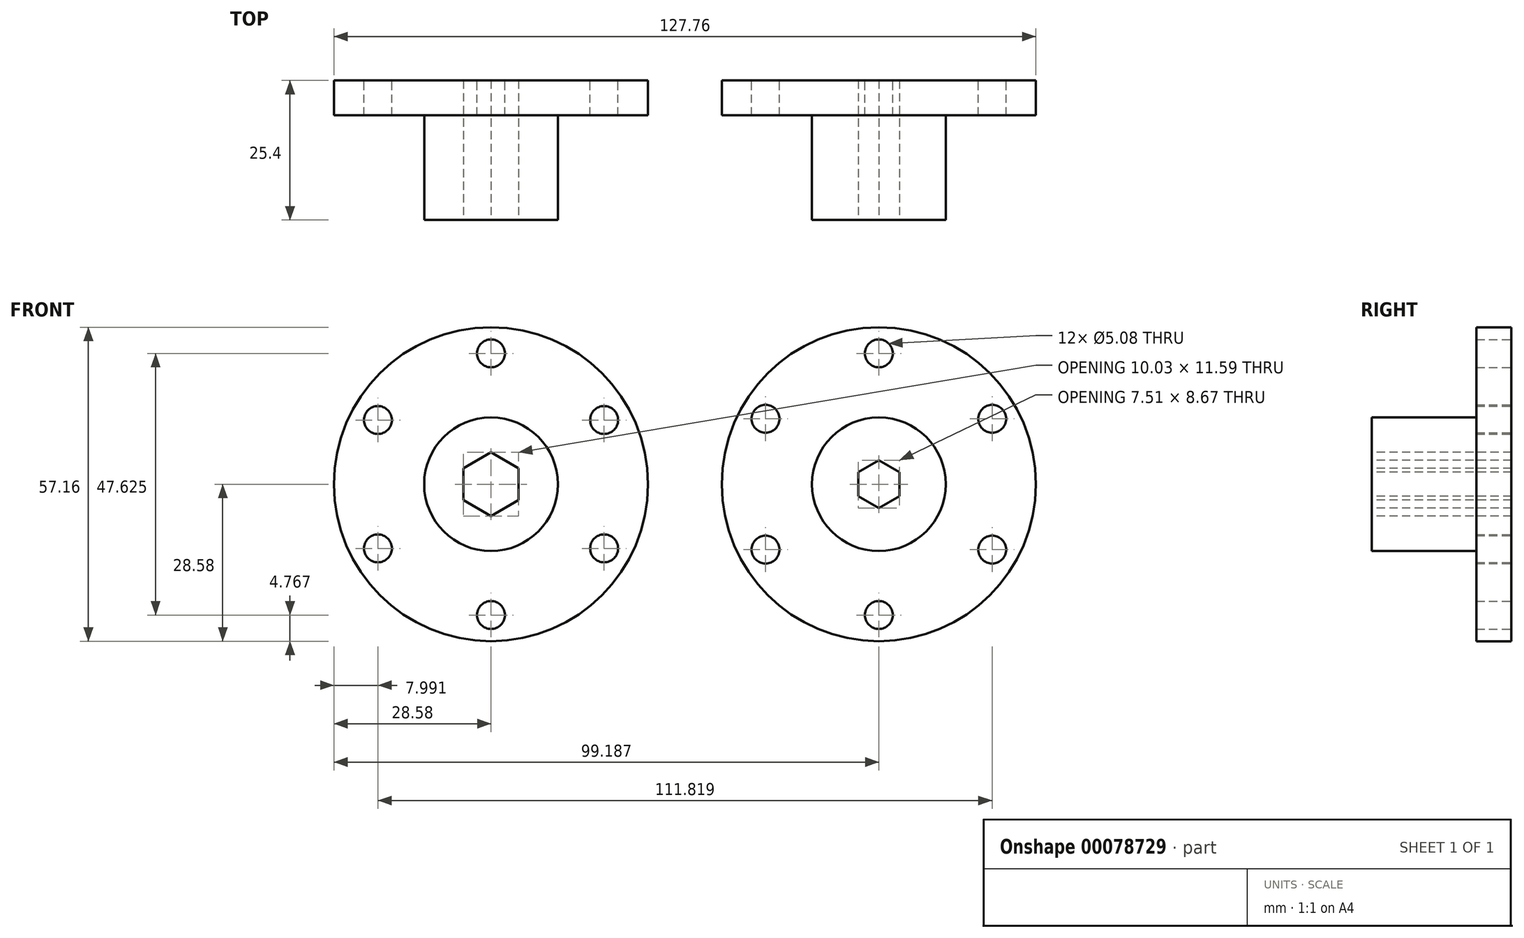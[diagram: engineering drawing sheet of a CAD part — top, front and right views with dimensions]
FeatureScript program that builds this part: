
annotation { "Feature Type Name" : "Feature", "Feature Type Description" : "" }
export const myFeature = defineFeature(function(context is Context, id is Id, definition is map)
    precondition{}
    {
        {
            var Q0;
            Q0=qCreatedBy(makeId("Front.planeOp"),FACE);
            var sketch = newSketch(context, id + "F0", { "sketchPlane" : qUnion([Q0])});
            skCircle(sketch, "E0", {"center": v(0, 0) * mm, "radius": 28.58 * mm});
            skCircle(sketch, "E1", {"center": v(0, 23.81) * mm, "radius": 2.54 * mm});
            skLineSegment(sketch, "E2", {"start": v(0, 23.81) * mm, "end": v(0, 0) * mm, "construction": true});
            skLineSegment(sketch, "E3", {"start": v(0, 0) * mm, "end": v(46.34, 26.76) * mm, "construction": true});
            skCircle(sketch, "E4", {"center": v(0, 0) * mm, "radius": 23.81 * mm, "construction": true});
            skCircle(sketch, "E5", {"center": v(20.59, 11.68) * mm, "radius": 2.54 * mm});
            skLineSegment(sketch, "E6", {"start": v(-28.58, 0) * mm, "end": v(30.98, 0) * mm, "construction": true});
            skCircle(sketch, "E7.MirrorC", {"center": v(0, -23.81) * mm, "radius": 2.54 * mm});
            skCircle(sketch, "E8.MirrorC", {"center": v(20.59, -11.68) * mm, "radius": 2.54 * mm});
            skCircle(sketch, "E9.MirrorC", {"center": v(-20.59, 11.68) * mm, "radius": 2.54 * mm});
            skCircle(sketch, "E10.MirrorC", {"center": v(-20.59, -11.68) * mm, "radius": 2.54 * mm});
            skCircle(sketch, "E11", {"center": v(70.6, 0) * mm, "radius": 28.58 * mm});
            skCircle(sketch, "E12", {"center": v(70.6, 23.81) * mm, "radius": 2.54 * mm});
            skCircle(sketch, "E13", {"center": v(70.6, 0) * mm, "radius": 23.81 * mm, "construction": true});
            skCircle(sketch, "E14.1.0", {"center": v(49.99, 11.9) * mm, "radius": 2.54 * mm});
            skCircle(sketch, "E14.2.0", {"center": v(49.99, -11.9) * mm, "radius": 2.54 * mm});
            skCircle(sketch, "E14.3.0", {"center": v(70.6, -23.81) * mm, "radius": 2.54 * mm});
            skCircle(sketch, "E14.4.0", {"center": v(91.23, -11.9) * mm, "radius": 2.54 * mm});
            skCircle(sketch, "E14.5.0", {"center": v(91.23, 11.9) * mm, "radius": 2.54 * mm});
            skSolve(sketch);
        }
        {
            var Q0;
            Q0 = qSketchRegion(id + "F0", true);
            extrude(context, id + "F1", {"entities" : qUnion([Q0]), "depth" : 6.35 * mm});
        }
        {
            var Q0;
            Q0=makeQuery(id+"F1.opExtrude","CAP_FACE",FACE,{"disambiguationData":[OSD([sQuery(id+"F0.wireOp",EDGE,"E0"),sQuery(id+"F0.wireOp",EDGE,"E1"),sQuery(id+"F0.wireOp",EDGE,"E5"),sQuery(id+"F0.wireOp",EDGE,"E7.MirrorC"),sQuery(id+"F0.wireOp",EDGE,"E8.MirrorC"),sQuery(id+"F0.wireOp",EDGE,"E9.MirrorC"),sQuery(id+"F0.wireOp",EDGE,"E10.MirrorC")])],"isStart":false});
            var sketch = newSketch(context, id + "F2", { "sketchPlane" : qUnion([Q0])});
            skCircle(sketch, "E15", {"center": v(0, 0) * mm, "radius": 12.17 * mm});
            skCircle(sketch, "E16", {"center": v(70.6, 0) * mm, "radius": 12.17 * mm});
            skSolve(sketch);
        }
        {
            var Q0;
            Q0 = qSketchRegion(id + "F2", true);
            extrude(context, id + "F3", {"entities" : qUnion([Q0]), "operationType" : NewBodyOperationType.ADD, "depth" : 19.05 * mm});
        }
        {
            var Q0;
            Q0=makeQuery(id+"F3.opExtrude","CAP_FACE",FACE,{"disambiguationData":[OSD([sQuery(id+"F2.wireOp",EDGE,"E15")])],"isStart":false});
            var sketch = newSketch(context, id + "F4", { "sketchPlane" : qUnion([Q0])});
            skCircle(sketch, "E17.cCircle", {"center": v(0, 0) * mm, "radius": 5.02 * mm, "construction": true});
            skLineSegment(sketch, "E17.0", {"start": v(-5.02, 2.9) * mm, "end": v(0, 5.8) * mm});
            skLineSegment(sketch, "E17.1", {"start": v(0, 5.8) * mm, "end": v(5.02, 2.9) * mm});
            skLineSegment(sketch, "E17.2", {"start": v(5.02, 2.9) * mm, "end": v(5.02, -2.9) * mm});
            skLineSegment(sketch, "E17.3", {"start": v(5.02, -2.9) * mm, "end": v(0, -5.8) * mm});
            skLineSegment(sketch, "E17.4", {"start": v(0, -5.8) * mm, "end": v(-5.02, -2.9) * mm});
            skLineSegment(sketch, "E17.5", {"start": v(-5.02, -2.9) * mm, "end": v(-5.02, 2.9) * mm});
            skPoint(sketch, "E17.0.midPoint", {"position": v(-2.5, 4.34) * mm});
            skLineSegment(sketch, "E18", {"start": v(0, 0) * mm, "end": v(2.5, 4.34) * mm, "construction": true});
            skCircle(sketch, "E19.cCircle", {"center": v(70.6, 0) * mm, "radius": 3.75 * mm, "construction": true});
            skLineSegment(sketch, "E19.0", {"start": v(70.6, 4.33) * mm, "end": v(74.36, 2.17) * mm});
            skLineSegment(sketch, "E19.1", {"start": v(74.36, 2.17) * mm, "end": v(74.36, -2.17) * mm});
            skLineSegment(sketch, "E19.2", {"start": v(74.36, -2.17) * mm, "end": v(70.6, -4.33) * mm});
            skLineSegment(sketch, "E19.3", {"start": v(70.6, -4.33) * mm, "end": v(66.85, -2.17) * mm});
            skLineSegment(sketch, "E19.4", {"start": v(66.85, -2.17) * mm, "end": v(66.85, 2.17) * mm});
            skLineSegment(sketch, "E19.5", {"start": v(66.85, 2.17) * mm, "end": v(70.6, 4.33) * mm});
            skPoint(sketch, "E19.0.midPoint", {"position": v(72.48, 3.25) * mm});
            skCircle(sketch, "E20.0.0", {"center": v(70.6, 0) * mm, "radius": 12.17 * mm});
            skSolve(sketch);
        }
        {
            var Q0;
            Q0=makeQuery(id+"F4.imprint","IMPRINT",FACE,{"disambiguationData":[TD([[makeQuery(id+"F4.imprint","IMPRINT",EDGE,{"derivedFrom":sQuery(id+"F4.wireOp",EDGE,"E17.0")}),-1.0]])]});
            var Q1;
            Q1=makeQuery(id+"F4.imprint","IMPRINT",FACE,{"disambiguationData":[TD([[makeQuery(id+"F4.imprint","IMPRINT",EDGE,{"derivedFrom":sQuery(id+"F4.wireOp",EDGE,"E19.0")}),-1.0]])]});
            extrude(context, id + "F5", {"entities" : qUnion([Q0, Q1]), "operationType" : NewBodyOperationType.REMOVE, "endBound" : BoundingType.THROUGH_ALL, "oppositeDirection" : true, "depth" : 25.4 * mm});
        }
        {
            var Q0;
            Q0=makeQuery(id+"F4.imprint","IMPRINT",FACE,{"disambiguationData":[TD([[makeQuery(id+"F4.imprint","IMPRINT",EDGE,{"derivedFrom":sQuery(id+"F4.wireOp",EDGE,"E19.0")}),-1.0]])]});
            extrude(context, id + "F6", {"entities" : qUnion([Q0]), "operationType" : NewBodyOperationType.REMOVE, "endBound" : BoundingType.THROUGH_ALL, "oppositeDirection" : true, "depth" : 25.4 * mm});
        }
    });
